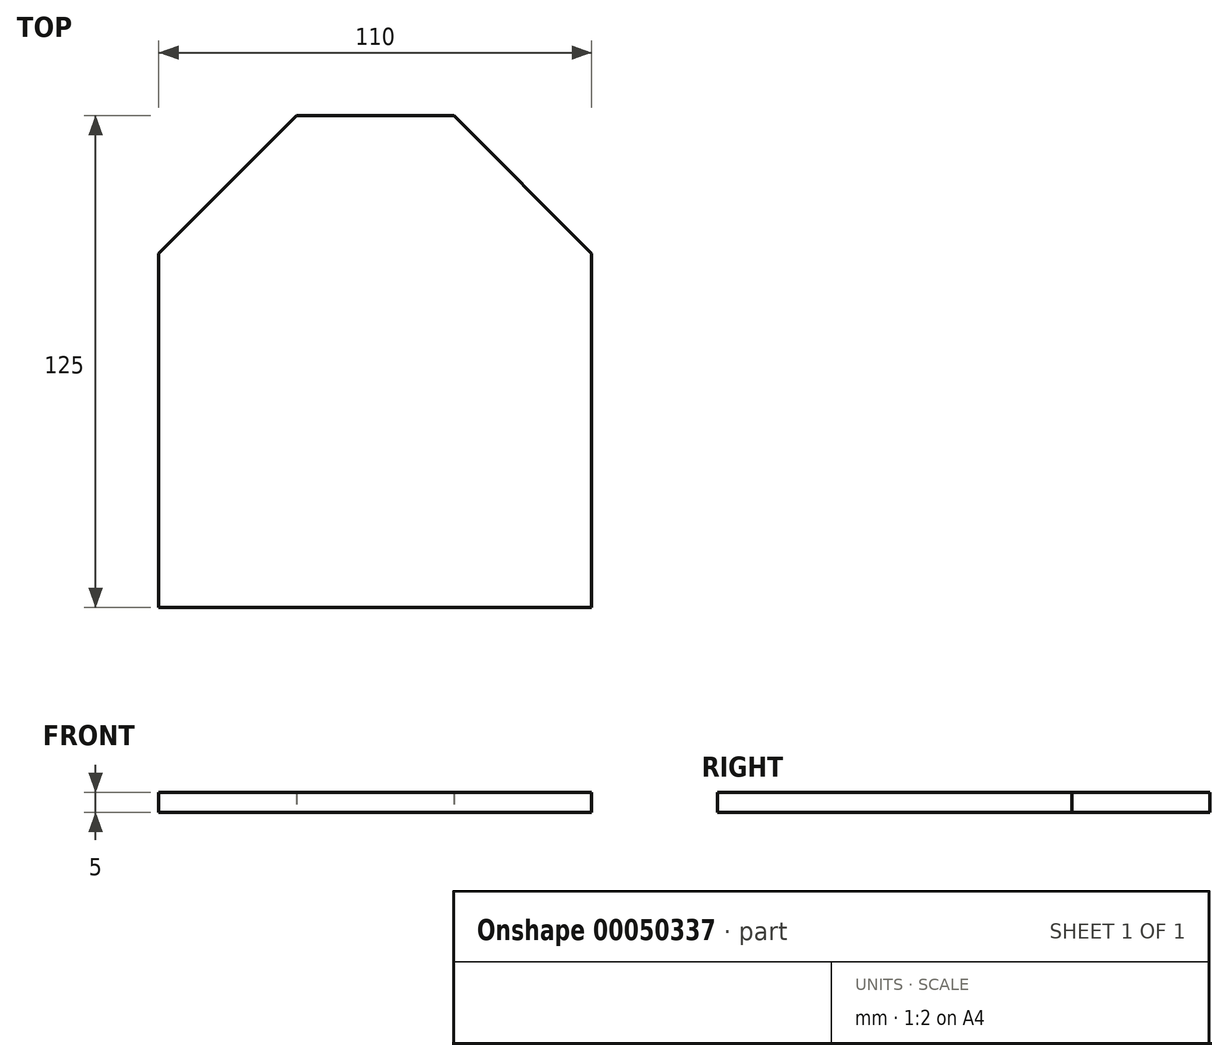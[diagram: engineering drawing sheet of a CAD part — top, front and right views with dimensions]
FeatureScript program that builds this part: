
annotation { "Feature Type Name" : "Feature", "Feature Type Description" : "" }
export const myFeature = defineFeature(function(context is Context, id is Id, definition is map)
    precondition{}
    {
        {
            var Q0;
            Q0=qCreatedBy(makeId("Top.planeOp"),FACE);
            var sketch = newSketch(context, id + "F0", { "sketchPlane" : qUnion([Q0])});
            skLineSegment(sketch, "E0", {"start": v(0, 62.5) * mm, "end": v(0, -62.5) * mm, "construction": true});
            skLineSegment(sketch, "E1", {"start": v(-55, 0) * mm, "end": v(55, 0) * mm, "construction": true});
            skLineSegment(sketch, "E2.bottom", {"start": v(-20, 62.5) * mm, "end": v(55, 62.5) * mm});
            skLineSegment(sketch, "E2.top", {"start": v(-55, -62.5) * mm, "end": v(55, -62.5) * mm});
            skLineSegment(sketch, "E2.left", {"start": v(-55, 27.5) * mm, "end": v(-55, -62.5) * mm});
            skLineSegment(sketch, "E2.right", {"start": v(55, 62.5) * mm, "end": v(55, -62.5) * mm});
            skLineSegment(sketch, "E3", {"start": v(-55, 27.5) * mm, "end": v(-20, 62.5) * mm});
            skLineSegment(sketch, "E4.MirrorCS", {"start": v(55, 27.5) * mm, "end": v(20, 62.5) * mm});
            skPoint(sketch, "E5.orphan", {"position": v(-55, 62.5) * mm});
            skSolve(sketch);
        }
        {
            var Q0;
            {var subQ1=sQuery(id+"F0.wireOp",EDGE,"E2.top");Q0=makeQuery(id+"F0.imprint","IMPRINT",FACE,{"disambiguationData":[TD([[makeQuery(id+"F0.imprint","IMPRINT",EDGE,{"derivedFrom":subQ1}),1.0]])]});}
            extrude(context, id + "F1", {"entities" : qUnion([Q0]), "depth" : 5 * mm});
        }
    });
